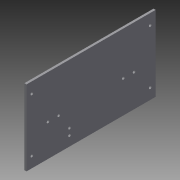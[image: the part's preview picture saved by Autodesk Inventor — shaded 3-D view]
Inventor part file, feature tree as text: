
AUTODESK INVENTOR PART (.ipt)
format: ipt  version: 2015 (Build 190159000, 159)  size: 117,248 bytes
history: native  units: in
note: dims shown in document units (in); Inventor stores cm internally (conversion verified against a paired STEP export)
features: sketch x4, extrude x2, hole x2, projected_geometry x2
ambient origin geometry x8: Origin, YZ Plane, XZ Plane, XY Plane, X Axis, Y Axis, Z Axis, Center Point
bodies: Solid1 (feature_tree)
feature tree (10):
  extrude  "Extrusion1"  Depth=6.0in
  hole  "Hole1"  [1 undecoded]
  hole  "Hole2"  [1 undecoded]
  extrude  "Extrusion2"  Depth=0.5in
  sketch  "Sketch1"  dims[d0=3.5in d1=6.0in]
  sketch  "Sketch2"  dims[d2=0.1in d3=0.0in d4=0.25in]
  projected_geometry  "Projected Loop1"
  sketch  "Sketch3"  dims[d5=0.5in d6=0.5in]
  projected_geometry  "Projected Loop2"
  sketch  "Sketch4"  dims[d7=0.5in d8=0.5in d9=0.125in d10=0.75in d11=0.375in d12=0.25in d13=0.5635in d14=1.0in d15=0.8108in d16=1.5in d17=1.0in d18=0.5in d19=0.5in d20=1.0in d21=0.125in d22=0.75in d23=0.375in d24=0.25in d25=0.5635in d26=1.0in d27=0.8108in d28=3.0in d29=1.5in d30=0.25in d31=1.0in d32=0.15in d33=0.5in d34=0.3in d35=0.125in d36=0.125in d37=1.0in d38=0.0in]
note: 2 required parameter values undecoded (feature->parameter linkage not recoverable at this tier; creation-order binding heuristic only, values carry confidence <= 0.55)
